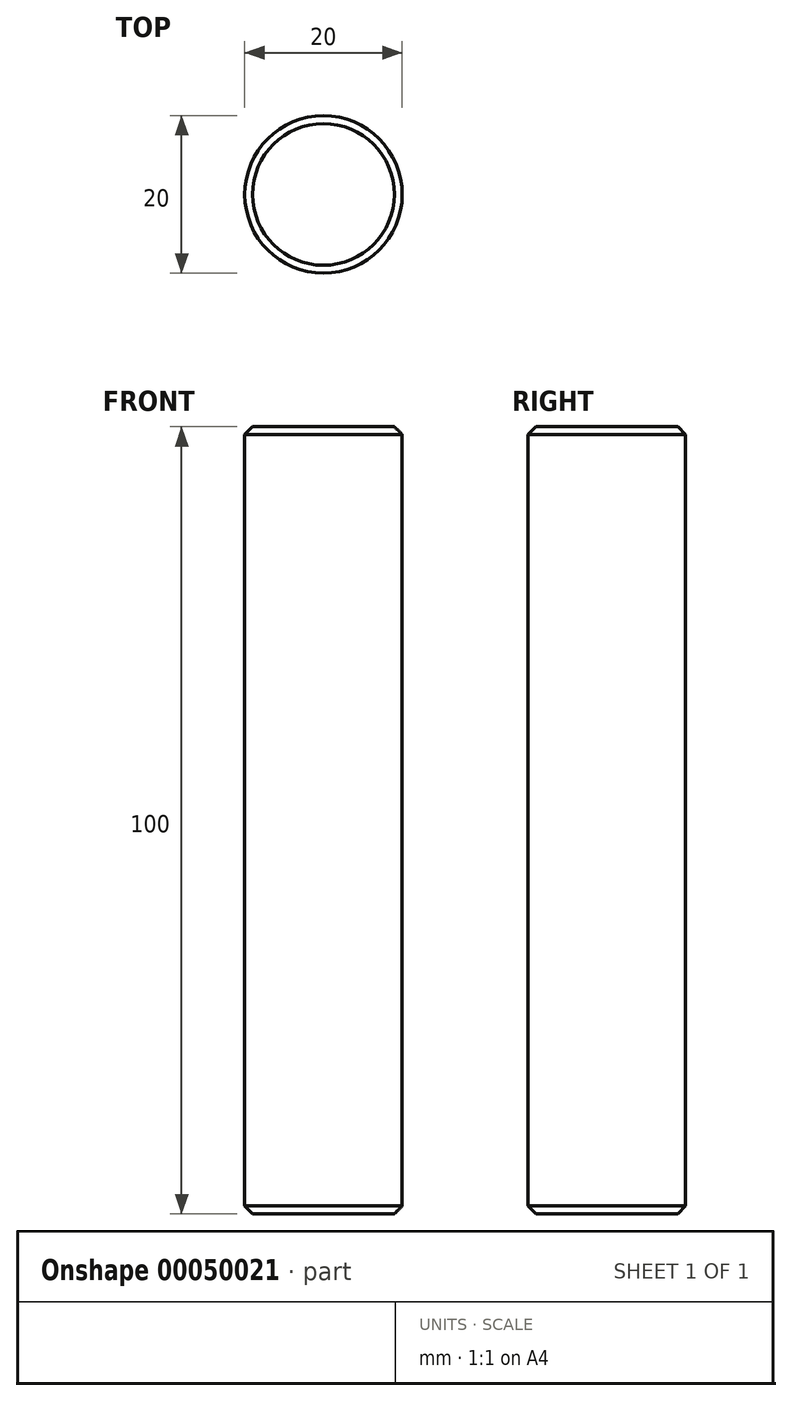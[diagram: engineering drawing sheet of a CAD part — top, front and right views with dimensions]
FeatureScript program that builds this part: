
annotation { "Feature Type Name" : "Feature", "Feature Type Description" : "" }
export const myFeature = defineFeature(function(context is Context, id is Id, definition is map)
    precondition{}
    {
        {
            var Q0;
            Q0=qCreatedBy(makeId("Top.planeOp"),FACE);
            var sketch = newSketch(context, id + "F0", { "sketchPlane" : qUnion([Q0])});
            skCircle(sketch, "E0", {"center": v(-11.81, 7.32) * mm, "radius": 10 * mm});
            skSolve(sketch);
        }
        {
            var Q0;
            Q0=makeQuery(id+"F0.imprint","IMPRINT",FACE,{"disambiguationData":[TD([[makeQuery(id+"F0.imprint","IMPRINT",EDGE,{"derivedFrom":sQuery(id+"F0.wireOp",EDGE,"E0")}),1.0]])]});
            extrude(context, id + "F1", {"entities" : qUnion([Q0]), "depth" : 100 * mm});
        }
        {
            var Q0;
            Q0=makeQuery(id+"F1.opExtrude","CAP_EDGE",EDGE,{"disambiguationData":[OSD([sQuery(id+"F0.wireOp",EDGE,"E0")])],"isStart":false});
            chamfer(context, id + "F2", {"entities" : qUnion([Q0]), "width" : 1 * mm, "tangentPropagation" : true});
        }
        {
            var Q0;
            Q0=makeQuery(id+"F1.opExtrude","CAP_EDGE",EDGE,{"disambiguationData":[OSD([sQuery(id+"F0.wireOp",EDGE,"E0")])],"isStart":true});
            chamfer(context, id + "F3", {"entities" : qUnion([Q0]), "width" : 1 * mm, "tangentPropagation" : true});
        }
    });
